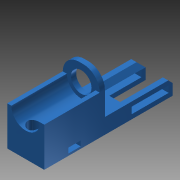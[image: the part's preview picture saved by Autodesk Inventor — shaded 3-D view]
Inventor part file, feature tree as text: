
AUTODESK INVENTOR PART (.ipt)
format: ipt  version: 2013 SP2 (Build 170200200, 200)  size: 194,560 bytes
history: native  units: in
note: dims shown in document units (in); Inventor stores cm internally (conversion verified against a paired STEP export)
features: extrude x10, sketch x8, fillet x1, chamfer x1
ambient origin geometry x8: Origin, YZ Plane, XZ Plane, XY Plane, X Axis, Y Axis, Z Axis, Center Point
bodies: Solid1 (feature_tree)
feature tree (20):
  sketch  "Sketch1"  dims[d5=1.063in d6=0.0in d11=0.5512in]
  extrude  "Extrusion1"  Depth=0.5512in
  extrude  "Extrusion6"  Depth=0.0787in
  extrude  "Extrusion5"  Depth=0.7087in
  extrude  "Extrusion7"  Depth=1.063in
  fillet  "Fillet1"  Radius=0.0984in
  extrude  "Extrusion8"  Depth=0.315in
  extrude  "Extrusion9"  Depth=0.0984in
  extrude  "Extrusion10"  Depth=0.0787in TaperAngle=0.0deg
  extrude  "Extrusion11"  Depth=1.2992in TaperAngle=0.0deg
  extrude  "Extrusion12"  Depth=1.1811in TaperAngle=0.0deg
  extrude  "Extrusion13"  Depth=0.9055in
  chamfer  "Chamfer2"  [1 undecoded]
  sketch  "Sketch3"  dims[d12=0.3937in d13=0.0787in]
  sketch  "Sketch4"  dims[d18=0.748in d19=0.7087in]
  sketch  "Sketch5"  dims[d20=1.1811in d21=0.0in d22=1.063in d25=0.0984in d26=0.0in]
  sketch  "Sketch6"  dims[d27=0.0787in d28=0.0in d29=0.315in]
  sketch  "Sketch7"  dims[d32=0.2362in d33=0.0984in]
  sketch  "Sketch8"  dims[d34=0.0394in d35=0.0787in d36=0.0in]
  sketch  "Sketch9"  dims[d37=0.2953in d38=1.2992in d39=0.0in d41=1.1811in d42=0.0in d45=0.9055in d47=0.0in d49=0.126in d51=0.3937in d52=0.0in d55=0.7087in d56=0.2362in d57=0.2362in d58=0.1575in d59=1.3386in d60=0.4331in d61=0.0in d62=0.126in d63=0.126in d64=0.1575in d65=0.0in d69=0.3307in d70=0.7874in d71=0.0866in d72=0.0787in d73=45.0deg]
note: 1 required parameter value undecoded (feature->parameter linkage not recoverable at this tier; creation-order binding heuristic only, values carry confidence <= 0.55)
